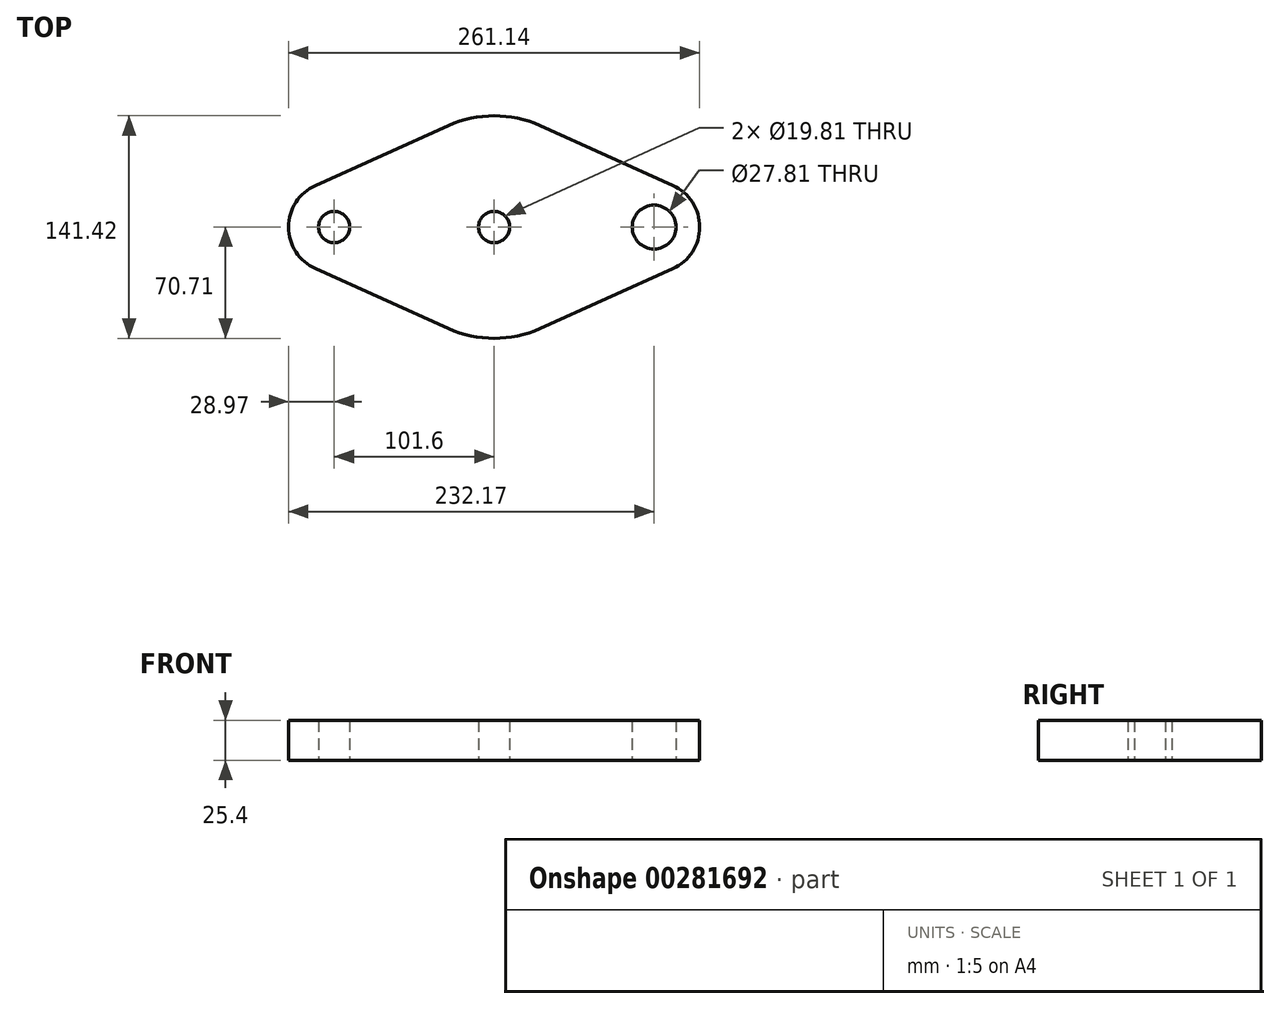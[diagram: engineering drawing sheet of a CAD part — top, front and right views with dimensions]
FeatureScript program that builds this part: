
annotation { "Feature Type Name" : "Feature", "Feature Type Description" : "" }
export const myFeature = defineFeature(function(context is Context, id is Id, definition is map)
    precondition{}
    {
        {
            var Q0;
            Q0=qCreatedBy(makeId("Top.planeOp"),FACE);
            var sketch = newSketch(context, id + "F0", { "sketchPlane" : qUnion([Q0])});
            skCircle(sketch, "E0", {"center": v(0, 0) * mm, "radius": 64.77 * mm});
            skCircle(sketch, "E1", {"center": v(0, 0) * mm, "radius": 70.7 * mm});
            skLineSegment(sketch, "E2", {"start": v(0, 0) * mm, "end": v(-101.6, 0) * mm});
            skCircle(sketch, "E3", {"center": v(-101.6, 0) * mm, "radius": 9.9 * mm});
            skCircle(sketch, "E4", {"center": v(-101.6, 0) * mm, "radius": 13.9 * mm});
            skLineSegment(sketch, "E5.MirrorCS", {"start": v(0, 0) * mm, "end": v(101.6, 0) * mm});
            skCircle(sketch, "E6.MirrorC", {"center": v(101.6, 0) * mm, "radius": 13.9 * mm});
            skCircle(sketch, "E7.MirrorC", {"center": v(101.6, 0) * mm, "radius": 9.9 * mm});
            skCircle(sketch, "E8", {"center": v(-101.6, 0) * mm, "radius": 28.97 * mm});
            skCircle(sketch, "E9.MirrorC", {"center": v(101.6, 0) * mm, "radius": 28.97 * mm});
            skLineSegment(sketch, "E10", {"start": v(-113.5, 26.41) * mm, "end": v(-29.05, 64.46) * mm});
            skLineSegment(sketch, "E11", {"start": v(-113.5, -26.41) * mm, "end": v(-29.05, -64.46) * mm});
            skLineSegment(sketch, "E12.MirrorCS", {"start": v(113.5, 26.41) * mm, "end": v(29.05, 64.46) * mm});
            skLineSegment(sketch, "E13.MirrorCS", {"start": v(113.5, -26.41) * mm, "end": v(29.05, -64.46) * mm});
            skCircle(sketch, "E14", {"center": v(0, 0) * mm, "radius": 9.9 * mm});
            skSolve(sketch);
        }
        {
            var Q0;
            Q0=qSketchRegion(id+"F0",true);
            var Q1;
            {var subQ0=sQuery(id+"F0.wireOp",EDGE,"E14");var subQ1=sQuery(id+"F0.wireOp",EDGE,"E2");var subQ2=makeQuery(id+"F0.imprint","INTERSECT",VERTEX,{"derivedFrom":[subQ1,subQ0]});Q1=makeQuery(id+"F0.imprint","IMPRINT",FACE,{"disambiguationData":[TD([[makeQuery(id+"F0.imprint","IMPRINT",EDGE,{"disambiguationData":[TD([[subQ2,-1.0]])],"derivedFrom":subQ1}),1.0]])]});}
            var Q2;
            {var subQ0=sQuery(id+"F0.wireOp",EDGE,"E14");var subQ1=sQuery(id+"F0.wireOp",EDGE,"E2");var subQ2=makeQuery(id+"F0.imprint","INTERSECT",VERTEX,{"derivedFrom":[subQ1,subQ0]});Q2=makeQuery(id+"F0.imprint","IMPRINT",FACE,{"disambiguationData":[TD([[makeQuery(id+"F0.imprint","IMPRINT",EDGE,{"disambiguationData":[TD([[subQ2,-1.0]])],"derivedFrom":subQ1}),-1.0]])]});}
            var Q3;
            Q3=makeQuery(id+"F0.imprint","IMPRINT",FACE,{"disambiguationData":[TD([[makeQuery(id+"F0.imprint","IMPRINT",EDGE,{"derivedFrom":sQuery(id+"F0.wireOp",EDGE,"E6.MirrorC")}),-1.0]])]});
            var Q4;
            Q4=makeQuery(id+"F0.imprint","IMPRINT",FACE,{"disambiguationData":[TD([[makeQuery(id+"F0.imprint","IMPRINT",EDGE,{"derivedFrom":sQuery(id+"F0.wireOp",EDGE,"E3")}),-1.0]])]});
            extrude(context, id + "F1", {"entities" : qUnion([Q0, Q1, Q2, Q3, Q4]), "depth" : 25.4 * mm});
        }
    });
